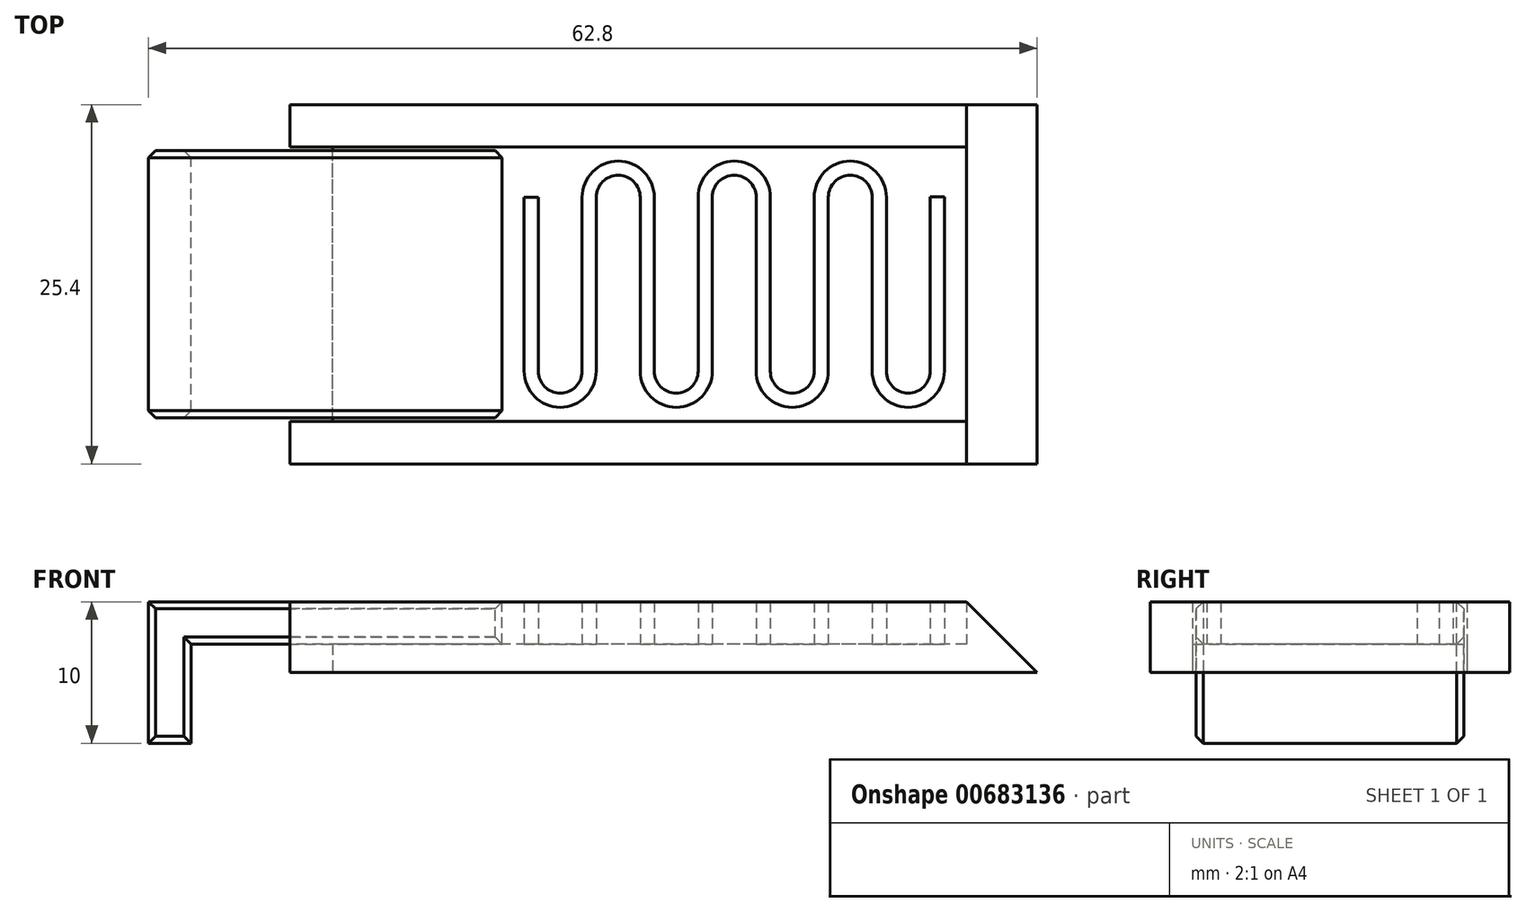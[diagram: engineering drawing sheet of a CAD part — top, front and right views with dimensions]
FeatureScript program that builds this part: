
annotation { "Feature Type Name" : "Feature", "Feature Type Description" : "" }
export const myFeature = defineFeature(function(context is Context, id is Id, definition is map)
    precondition{}
    {
        {
            var Q0;
            Q0=qCreatedBy(makeId("Top.planeOp"),FACE);
            var sketch = newSketch(context, id + "F0", { "sketchPlane" : qUnion([Q0])});
            skLineSegment(sketch, "E0.bottom", {"start": v(25.4, -12.7) * mm, "end": v(-25.4, -12.7) * mm});
            skLineSegment(sketch, "E0.top", {"start": v(25.4, 12.7) * mm, "end": v(-25.4, 12.7) * mm});
            skLineSegment(sketch, "E0.left", {"start": v(25.4, -12.7) * mm, "end": v(25.4, 12.7) * mm});
            skLineSegment(sketch, "E0.right", {"start": v(-25.4, -12.7) * mm, "end": v(-25.4, 12.7) * mm});
            skPoint(sketch, "E0.middle", {"position": v(0, 0) * mm});
            skSolve(sketch);
        }
        {
            var Q0;
            Q0=makeQuery(id+"F0.imprint","IMPRINT",FACE,{"disambiguationData":[TD([[makeQuery(id+"F0.imprint","IMPRINT",EDGE,{"derivedFrom":sQuery(id+"F0.wireOp",EDGE,"E0.bottom")}),-1.0]])]});
            extrude(context, id + "F1", {"entities" : qUnion([Q0]), "depth" : 2 * mm, "offsetDistance" : 25 * mm});
        }
        {
            var Q0;
            Q0=makeQuery(id+"F1.opExtrude","CAP_FACE",FACE,{"disambiguationData":[OSD([sQuery(id+"F0.wireOp",EDGE,"E0.bottom"),sQuery(id+"F0.wireOp",EDGE,"E0.top"),sQuery(id+"F0.wireOp",EDGE,"E0.left"),sQuery(id+"F0.wireOp",EDGE,"E0.right")])],"isStart":false});
            var sketch = newSketch(context, id + "F2", { "sketchPlane" : qUnion([Q0])});
            skLineSegment(sketch, "E1", {"start": v(-25.4, 9.7) * mm, "end": v(25.4, 9.7) * mm});
            skLineSegment(sketch, "E2", {"start": v(25.4, 9.7) * mm, "end": v(25.4, 9.7) * mm});
            skLineSegment(sketch, "E3", {"start": v(25.4, -9.7) * mm, "end": v(-25.4, -9.7) * mm});
            skSolve(sketch);
        }
        {
            var Q0;
            {var subQ0=sQuery(id+"F2.wireOp",EDGE,"E1");Q0=makeQuery(id+"F2.imprint","IMPRINT",FACE,{"disambiguationData":[TD([[makeQuery(id+"F2.imprint","IMPRINT",EDGE,{"derivedFrom":subQ0}),1.0]])]});}
            var Q1;
            {var subQ0=sQuery(id+"F2.wireOp",EDGE,"E3");Q1=makeQuery(id+"F2.imprint","IMPRINT",FACE,{"disambiguationData":[TD([[makeQuery(id+"F2.imprint","IMPRINT",EDGE,{"derivedFrom":subQ0}),1.0]])]});}
            extrude(context, id + "F3", {"entities" : qUnion([Q0, Q1]), "operationType" : NewBodyOperationType.ADD, "depth" : 3 * mm, "offsetDistance" : 25 * mm});
        }
        {
            var Q0;
            {var subQ0=sQuery(id+"F0.wireOp",EDGE,"E0.bottom");Q0=makeQuery(id+"F3.boolean.opBoolean","MERGE",FACE,{"derivedFrom":[makeQuery(id+"F1.opExtrude","SWEPT_FACE",FACE,{"disambiguationData":[OSD([subQ0])]}),makeQuery(id+"F3.opExtrude","SWEPT_FACE",FACE,{"disambiguationData":[OSD([subQ0])]})]});}
            var sketch = newSketch(context, id + "F4", { "sketchPlane" : qUnion([Q0])});
            skLineSegment(sketch, "E4", {"start": v(25.4, 5) * mm, "end": v(25.4, 0) * mm});
            skLineSegment(sketch, "E5", {"start": v(25.4, 5) * mm, "end": v(30.4, 0) * mm});
            skLineSegment(sketch, "E6", {"start": v(30.4, 0) * mm, "end": v(25.4, 0) * mm});
            skSolve(sketch);
        }
        {
            var Q0;
            Q0=makeQuery(id+"F4.imprint","IMPRINT",FACE,{"disambiguationData":[TD([[makeQuery(id+"F4.imprint","IMPRINT",EDGE,{"derivedFrom":sQuery(id+"F4.wireOp",EDGE,"E4")}),1.0]])]});
            extrude(context, id + "F5", {"entities" : qUnion([Q0]), "operationType" : NewBodyOperationType.ADD, "oppositeDirection" : true, "depth" : 25.4 * mm, "offsetDistance" : 25 * mm});
        }
        {
            var Q0;
            {var subQ0=sQuery(id+"F0.wireOp",EDGE,"E0.right");var subQ1=makeQuery(id+"F1.opExtrude","CAP_EDGE",EDGE,{"disambiguationData":[OSD([subQ0])],"isStart":false});Q0=makeQuery(id+"F3.boolean.opBoolean","MERGE",FACE,{"derivedFrom":[makeQuery(id+"F1.opExtrude","SWEPT_FACE",FACE,{"disambiguationData":[OSD([subQ0])]}),makeQuery(id+"F3.opExtrude","SWEPT_FACE",FACE,{"disambiguationData":[OSD([subQ0]),TDD([makeQuery(id+"F2.imprint","IMPRINT",EDGE,{"disambiguationData":[TD([[makeQuery(id+"F2.imprint","INTERSECT",VERTEX,{"derivedFrom":[makeQuery(id+"F1.opExtrude","CAP_EDGE",EDGE,{"disambiguationData":[OSD([sQuery(id+"F0.wireOp",EDGE,"E0.bottom")])],"isStart":false}),subQ1]}),-1.0]])],"derivedFrom":subQ1})])]}),makeQuery(id+"F3.opExtrude","SWEPT_FACE",FACE,{"disambiguationData":[OSD([subQ0]),TDD([makeQuery(id+"F2.imprint","IMPRINT",EDGE,{"disambiguationData":[TD([[makeQuery(id+"F2.imprint","INTERSECT",VERTEX,{"derivedFrom":[makeQuery(id+"F1.opExtrude","CAP_EDGE",EDGE,{"disambiguationData":[OSD([sQuery(id+"F0.wireOp",EDGE,"E0.top")])],"isStart":false}),subQ1]}),1.0]])],"derivedFrom":subQ1})])]})]});}
            extrude(context, id + "F6", {"entities" : qUnion([Q0]), "operationType" : NewBodyOperationType.REMOVE, "oppositeDirection" : true, "depth" : 3 * mm, "offsetDistance" : 25 * mm});
        }
        {
            var Q0;
            Q0=makeQuery(id+"F6.boolean.opBoolean","COPY",FACE,{"derivedFrom":makeQuery(id+"F6.opExtrude","CAP_FACE",FACE,{"disambiguationData":[OSD([sQuery(id+"F0.wireOp",EDGE,"E0.right")])],"isStart":false})});
            var sketch = newSketch(context, id + "F7", { "sketchPlane" : qUnion([Q0])});
            skLineSegment(sketch, "E7.bottom", {"start": v(9.7, 2) * mm, "end": v(-9.7, 2) * mm});
            skLineSegment(sketch, "E7.top", {"start": v(9.7, 0) * mm, "end": v(-9.7, 0) * mm});
            skLineSegment(sketch, "E7.left", {"start": v(9.7, 2) * mm, "end": v(9.7, 0) * mm});
            skLineSegment(sketch, "E7.right", {"start": v(-9.7, 2) * mm, "end": v(-9.7, 0) * mm});
            skSolve(sketch);
        }
        {
            var Q0;
            Q0 = qSketchRegion(id + "F7", true);
            extrude(context, id + "F8", {"entities" : qUnion([Q0]), "operationType" : NewBodyOperationType.REMOVE, "oppositeDirection" : true, "depth" : 3 * mm, "offsetDistance" : 25 * mm});
        }
        {
            var Q0;
            Q0=makeQuery(id+"F1.opExtrude","CAP_FACE",FACE,{"disambiguationData":[OSD([sQuery(id+"F0.wireOp",EDGE,"E0.bottom"),sQuery(id+"F0.wireOp",EDGE,"E0.top"),sQuery(id+"F0.wireOp",EDGE,"E0.left"),sQuery(id+"F0.wireOp",EDGE,"E0.right")])],"isStart":false});
            var sketch = newSketch(context, id + "F9", { "sketchPlane" : qUnion([Q0])});
            skLineSegment(sketch, "E8.bottom", {"start": v(-7.4, 9.45) * mm, "end": v(-32.4, 9.45) * mm});
            skLineSegment(sketch, "E8.top", {"start": v(-7.4, -9.45) * mm, "end": v(-32.4, -9.45) * mm});
            skLineSegment(sketch, "E8.left", {"start": v(-7.4, 9.45) * mm, "end": v(-7.4, -9.45) * mm});
            skLineSegment(sketch, "E8.right", {"start": v(-32.4, 9.45) * mm, "end": v(-32.4, -9.45) * mm});
            skSolve(sketch);
        }
        {
            var Q0;
            {var subQ0=sQuery(id+"F9.wireOp",EDGE,"E8.right");Q0=makeQuery(id+"F9.imprint","IMPRINT",FACE,{"disambiguationData":[TD([[makeQuery(id+"F9.imprint","IMPRINT",EDGE,{"derivedFrom":subQ0}),1.0]])]});}
            var Q1;
            {var subQ0=sQuery(id+"F9.wireOp",EDGE,"E8.left");Q1=makeQuery(id+"F9.imprint","IMPRINT",FACE,{"disambiguationData":[TD([[makeQuery(id+"F9.imprint","IMPRINT",EDGE,{"derivedFrom":subQ0}),-1.0]])]});}
            extrude(context, id + "F10", {"entities" : qUnion([Q0, Q1]), "depth" : 3 * mm, "offsetDistance" : 25 * mm});
        }
        {
            var Q0;
            Q0=makeQuery(id+"F10.opExtrude","CAP_FACE",FACE,{"disambiguationData":[OSD([sQuery(id+"F9.wireOp",EDGE,"E8.bottom"),sQuery(id+"F9.wireOp",EDGE,"E8.top"),sQuery(id+"F9.wireOp",EDGE,"E8.left"),sQuery(id+"F9.wireOp",EDGE,"E8.right")])],"isStart":true});
            var sketch = newSketch(context, id + "F11", { "sketchPlane" : qUnion([Q0])});
            skLineSegment(sketch, "E9.bottom", {"start": v(-32.4, 9.45) * mm, "end": v(-29.4, 9.45) * mm});
            skLineSegment(sketch, "E9.top", {"start": v(-32.4, -9.45) * mm, "end": v(-29.4, -9.45) * mm});
            skLineSegment(sketch, "E9.left", {"start": v(-32.4, 9.45) * mm, "end": v(-32.4, -9.45) * mm});
            skLineSegment(sketch, "E9.right", {"start": v(-29.4, 9.45) * mm, "end": v(-29.4, -9.45) * mm});
            skSolve(sketch);
        }
        {
            var Q0;
            Q0=makeQuery(id+"F11.imprint","IMPRINT",FACE,{"disambiguationData":[TD([[makeQuery(id+"F11.imprint","IMPRINT",EDGE,{"derivedFrom":sQuery(id+"F11.wireOp",EDGE,"E9.bottom")}),1.0]])]});
            extrude(context, id + "F12", {"entities" : qUnion([Q0]), "operationType" : NewBodyOperationType.ADD, "depth" : 7 * mm, "offsetDistance" : 25 * mm});
        }
        {
            var Q0;
            Q0=makeQuery(id+"F1.opExtrude","CAP_FACE",FACE,{"disambiguationData":[OSD([sQuery(id+"F0.wireOp",EDGE,"E0.bottom"),sQuery(id+"F0.wireOp",EDGE,"E0.top"),sQuery(id+"F0.wireOp",EDGE,"E0.left"),sQuery(id+"F0.wireOp",EDGE,"E0.right")])],"isStart":false});
            var sketch = newSketch(context, id + "F13", { "sketchPlane" : qUnion([Q0])});
            skLineSegment(sketch, "E10.bottom", {"start": v(25.4, -8.7) * mm, "end": v(-7.4, -8.7) * mm});
            skLineSegment(sketch, "E10.top", {"start": v(25.4, 8.7) * mm, "end": v(-7.4, 8.7) * mm});
            skLineSegment(sketch, "E10.left", {"start": v(25.4, -8.7) * mm, "end": v(25.4, 8.7) * mm});
            skLineSegment(sketch, "E10.right", {"start": v(-7.4, -8.7) * mm, "end": v(-7.4, 8.7) * mm});
            skPoint(sketch, "E10.middle", {"position": v(9, 0) * mm});
            skLineSegment(sketch, "E11", {"start": v(9, 0) * mm, "end": v(-7.4, 0) * mm, "construction": true});
            skLineSegment(sketch, "E12", {"start": v(0.8, 0) * mm, "end": v(0.8, 8.7) * mm, "construction": true});
            skLineSegment(sketch, "E13", {"start": v(0.8, 0) * mm, "end": v(0.8, -8.7) * mm, "construction": true});
            skCircle(sketch, "E14", {"center": v(9, 6.15) * mm, "radius": 2.55 * mm});
            skCircle(sketch, "E15", {"center": v(9, 6.15) * mm, "radius": 1.55 * mm});
            skCircle(sketch, "E16", {"center": v(0.8, 6.15) * mm, "radius": 2.55 * mm});
            skCircle(sketch, "E17", {"center": v(0.8, 6.15) * mm, "radius": 1.55 * mm});
            skCircle(sketch, "E18", {"center": v(17.2, 6.15) * mm, "radius": 2.55 * mm});
            skCircle(sketch, "E19", {"center": v(17.2, 6.15) * mm, "radius": 1.55 * mm});
            skCircle(sketch, "E20", {"center": v(4.9, -6.15) * mm, "radius": 2.55 * mm});
            skCircle(sketch, "E21", {"center": v(4.9, -6.15) * mm, "radius": 1.55 * mm});
            skCircle(sketch, "E22", {"center": v(13.1, -6.15) * mm, "radius": 2.55 * mm});
            skCircle(sketch, "E23", {"center": v(13.1, -6.15) * mm, "radius": 1.55 * mm});
            skCircle(sketch, "E24", {"center": v(-3.3, -6.15) * mm, "radius": 1.55 * mm});
            skCircle(sketch, "E25", {"center": v(-3.3, -6.15) * mm, "radius": 2.55 * mm});
            skLineSegment(sketch, "E26.bottom", {"start": v(0.8, 6.15) * mm, "end": v(0.8, 6.15) * mm});
            skLineSegment(sketch, "E26.top", {"start": v(0.8, 6.15) * mm, "end": v(0.8, 6.15) * mm});
            skLineSegment(sketch, "E26.left", {"start": v(0.8, 6.15) * mm, "end": v(0.8, 6.15) * mm});
            skLineSegment(sketch, "E26.right", {"start": v(0.8, 6.15) * mm, "end": v(0.8, 6.15) * mm});
            skLineSegment(sketch, "E27.bottom", {"start": v(-0.75, 6.15) * mm, "end": v(-1.75, 6.15) * mm});
            skLineSegment(sketch, "E27.top", {"start": v(-0.75, -6.15) * mm, "end": v(-1.75, -6.15) * mm});
            skLineSegment(sketch, "E27.left", {"start": v(-0.75, 6.15) * mm, "end": v(-0.75, -6.15) * mm});
            skLineSegment(sketch, "E27.right", {"start": v(-1.75, 6.15) * mm, "end": v(-1.75, -6.15) * mm});
            skLineSegment(sketch, "E28.bottom", {"start": v(2.35, 6.15) * mm, "end": v(3.35, 6.15) * mm});
            skLineSegment(sketch, "E28.top", {"start": v(2.35, -6.15) * mm, "end": v(3.35, -6.15) * mm});
            skLineSegment(sketch, "E28.left", {"start": v(2.35, 6.15) * mm, "end": v(2.35, -6.15) * mm});
            skLineSegment(sketch, "E28.right", {"start": v(3.35, 6.15) * mm, "end": v(3.35, -6.15) * mm});
            skLineSegment(sketch, "E29.bottom", {"start": v(7.45, 6.15) * mm, "end": v(6.45, 6.15) * mm});
            skLineSegment(sketch, "E29.top", {"start": v(7.45, -6.15) * mm, "end": v(6.45, -6.15) * mm});
            skLineSegment(sketch, "E29.left", {"start": v(7.45, 6.15) * mm, "end": v(7.45, -6.15) * mm});
            skLineSegment(sketch, "E29.right", {"start": v(6.45, 6.15) * mm, "end": v(6.45, -6.15) * mm});
            skLineSegment(sketch, "E30.bottom", {"start": v(10.55, 6.15) * mm, "end": v(11.55, 6.15) * mm});
            skLineSegment(sketch, "E30.top", {"start": v(10.55, -6.15) * mm, "end": v(11.55, -6.15) * mm});
            skLineSegment(sketch, "E30.left", {"start": v(10.55, 6.15) * mm, "end": v(10.55, -6.15) * mm});
            skLineSegment(sketch, "E30.right", {"start": v(11.55, 6.15) * mm, "end": v(11.55, -6.15) * mm});
            skLineSegment(sketch, "E31.bottom", {"start": v(15.65, 6.15) * mm, "end": v(14.65, 6.15) * mm});
            skLineSegment(sketch, "E31.top", {"start": v(15.65, -6.15) * mm, "end": v(14.65, -6.15) * mm});
            skLineSegment(sketch, "E31.left", {"start": v(15.65, 6.15) * mm, "end": v(15.65, -6.15) * mm});
            skLineSegment(sketch, "E31.right", {"start": v(14.65, 6.15) * mm, "end": v(14.65, -6.15) * mm});
            skLineSegment(sketch, "E32.bottom", {"start": v(18.75, 6.15) * mm, "end": v(19.75, 6.15) * mm});
            skLineSegment(sketch, "E32.top", {"start": v(18.75, -6.15) * mm, "end": v(19.75, -6.15) * mm});
            skLineSegment(sketch, "E32.left", {"start": v(18.75, 6.15) * mm, "end": v(18.75, -6.15) * mm});
            skLineSegment(sketch, "E32.right", {"start": v(19.75, 6.15) * mm, "end": v(19.75, -6.15) * mm});
            skLineSegment(sketch, "E33.bottom", {"start": v(-4.85, 6.15) * mm, "end": v(-5.85, 6.15) * mm});
            skLineSegment(sketch, "E33.top", {"start": v(-4.85, -6.15) * mm, "end": v(-5.85, -6.15) * mm});
            skLineSegment(sketch, "E33.left", {"start": v(-4.85, 6.15) * mm, "end": v(-4.85, -6.15) * mm});
            skLineSegment(sketch, "E33.right", {"start": v(-5.85, 6.15) * mm, "end": v(-5.85, -6.15) * mm});
            skLineSegment(sketch, "E34.bottom", {"start": v(-7.4, 8.7) * mm, "end": v(-5.85, 8.7) * mm});
            skLineSegment(sketch, "E34.top", {"start": v(-7.4, 3.6) * mm, "end": v(-5.85, 3.6) * mm});
            skLineSegment(sketch, "E34.left", {"start": v(-7.4, 8.7) * mm, "end": v(-7.4, 3.6) * mm});
            skLineSegment(sketch, "E34.right", {"start": v(-5.85, 8.7) * mm, "end": v(-5.85, 3.6) * mm});
            skCircle(sketch, "E35", {"center": v(21.3, -6.15) * mm, "radius": 2.55 * mm});
            skCircle(sketch, "E36", {"center": v(21.3, -6.15) * mm, "radius": 1.55 * mm});
            skLineSegment(sketch, "E37.bottom", {"start": v(22.85, -6.15) * mm, "end": v(23.85, -6.15) * mm});
            skLineSegment(sketch, "E37.top", {"start": v(22.85, 6.16) * mm, "end": v(23.85, 6.16) * mm});
            skLineSegment(sketch, "E37.left", {"start": v(22.85, -6.15) * mm, "end": v(22.85, 6.16) * mm});
            skLineSegment(sketch, "E37.right", {"start": v(23.85, -6.15) * mm, "end": v(23.85, 6.16) * mm});
            skLineSegment(sketch, "E38.bottom", {"start": v(23.85, 6.16) * mm, "end": v(23.85, 6.16) * mm});
            skLineSegment(sketch, "E38.top", {"start": v(23.85, 6.16) * mm, "end": v(23.85, 6.16) * mm});
            skLineSegment(sketch, "E38.left", {"start": v(23.85, 6.16) * mm, "end": v(23.85, 6.16) * mm});
            skLineSegment(sketch, "E38.right", {"start": v(23.85, 6.16) * mm, "end": v(23.85, 6.16) * mm});
            skLineSegment(sketch, "E39.bottom", {"start": v(25.4, 8.7) * mm, "end": v(23.85, 8.7) * mm});
            skLineSegment(sketch, "E39.top", {"start": v(25.4, 3.6) * mm, "end": v(23.85, 3.6) * mm});
            skLineSegment(sketch, "E39.left", {"start": v(25.4, 8.7) * mm, "end": v(25.4, 3.6) * mm});
            skLineSegment(sketch, "E39.right", {"start": v(23.85, 8.7) * mm, "end": v(23.85, 3.6) * mm});
            skSolve(sketch);
        }
        {
            var Q0;
            {var subQ1=sQuery(id+"F13.wireOp",EDGE,"E34.bottom");Q0=makeQuery(id+"F13.imprint","IMPRINT",FACE,{"disambiguationData":[TD([[makeQuery(id+"F13.imprint","IMPRINT",EDGE,{"derivedFrom":subQ1}),-1.0]])]});}
            var Q1;
            {var subQ2=sQuery(id+"F13.wireOp",EDGE,"E33.bottom");Q1=makeQuery(id+"F13.imprint","IMPRINT",FACE,{"disambiguationData":[TD([[makeQuery(id+"F13.imprint","IMPRINT",EDGE,{"derivedFrom":subQ2}),1.0]])]});}
            var Q2;
            {var subQ1=sQuery(id+"F13.wireOp",EDGE,"E16");var subQ3=sQuery(id+"F13.wireOp",EDGE,"E27.left");var subQ4=makeQuery(id+"F13.imprint","INTERSECT",VERTEX,{"derivedFrom":[subQ1,subQ3]});Q2=makeQuery(id+"F13.imprint","IMPRINT",FACE,{"disambiguationData":[TD([[makeQuery(id+"F13.imprint","IMPRINT",EDGE,{"disambiguationData":[TD([[subQ4,1.0]])],"derivedFrom":subQ1}),-1.0]])]});}
            var Q3;
            {var subQ0=sQuery(id+"F13.wireOp",EDGE,"E33.top");Q3=makeQuery(id+"F13.imprint","IMPRINT",FACE,{"disambiguationData":[TD([[makeQuery(id+"F13.imprint","IMPRINT",EDGE,{"derivedFrom":subQ0}),-1.0]])]});}
            var Q4;
            {var subQ0=sQuery(id+"F13.wireOp",EDGE,"E27.top");Q4=makeQuery(id+"F13.imprint","IMPRINT",FACE,{"disambiguationData":[TD([[makeQuery(id+"F13.imprint","IMPRINT",EDGE,{"derivedFrom":subQ0}),-1.0]])]});}
            var Q5;
            {var subQ0=sQuery(id+"F13.wireOp",EDGE,"E27.top");Q5=makeQuery(id+"F13.imprint","IMPRINT",FACE,{"disambiguationData":[TD([[makeQuery(id+"F13.imprint","IMPRINT",EDGE,{"derivedFrom":subQ0}),1.0]])]});}
            var Q6;
            {var subQ0=sQuery(id+"F13.wireOp",EDGE,"E27.bottom");Q6=makeQuery(id+"F13.imprint","IMPRINT",FACE,{"disambiguationData":[TD([[makeQuery(id+"F13.imprint","IMPRINT",EDGE,{"derivedFrom":subQ0}),-1.0]])]});}
            var Q7;
            {var subQ0=sQuery(id+"F13.wireOp",EDGE,"E27.bottom");Q7=makeQuery(id+"F13.imprint","IMPRINT",FACE,{"disambiguationData":[TD([[makeQuery(id+"F13.imprint","IMPRINT",EDGE,{"derivedFrom":subQ0}),1.0]])]});}
            var Q8;
            {var subQ0=sQuery(id+"F13.wireOp",EDGE,"E28.bottom");Q8=makeQuery(id+"F13.imprint","IMPRINT",FACE,{"disambiguationData":[TD([[makeQuery(id+"F13.imprint","IMPRINT",EDGE,{"derivedFrom":subQ0}),-1.0]])]});}
            var Q9;
            {var subQ1=sQuery(id+"F13.wireOp",EDGE,"E16");var subQ3=sQuery(id+"F13.wireOp",EDGE,"E28.left");var subQ4=makeQuery(id+"F13.imprint","INTERSECT",VERTEX,{"derivedFrom":[subQ1,subQ3]});Q9=makeQuery(id+"F13.imprint","IMPRINT",FACE,{"disambiguationData":[TD([[makeQuery(id+"F13.imprint","IMPRINT",EDGE,{"disambiguationData":[TD([[subQ4,-1.0]])],"derivedFrom":subQ1}),-1.0]])]});}
            var Q10;
            {var subQ0=sQuery(id+"F13.wireOp",EDGE,"E28.top");Q10=makeQuery(id+"F13.imprint","IMPRINT",FACE,{"disambiguationData":[TD([[makeQuery(id+"F13.imprint","IMPRINT",EDGE,{"derivedFrom":subQ0}),-1.0]])]});}
            var Q11;
            {var subQ1=sQuery(id+"F13.wireOp",EDGE,"E14");var subQ3=sQuery(id+"F13.wireOp",EDGE,"E29.left");var subQ4=makeQuery(id+"F13.imprint","INTERSECT",VERTEX,{"derivedFrom":[subQ1,subQ3]});Q11=makeQuery(id+"F13.imprint","IMPRINT",FACE,{"disambiguationData":[TD([[makeQuery(id+"F13.imprint","IMPRINT",EDGE,{"disambiguationData":[TD([[subQ4,1.0]])],"derivedFrom":subQ1}),-1.0]])]});}
            var Q12;
            {var subQ0=sQuery(id+"F13.wireOp",EDGE,"E29.bottom");Q12=makeQuery(id+"F13.imprint","IMPRINT",FACE,{"disambiguationData":[TD([[makeQuery(id+"F13.imprint","IMPRINT",EDGE,{"derivedFrom":subQ0}),-1.0]])]});}
            var Q13;
            {var subQ0=sQuery(id+"F13.wireOp",EDGE,"E29.bottom");Q13=makeQuery(id+"F13.imprint","IMPRINT",FACE,{"disambiguationData":[TD([[makeQuery(id+"F13.imprint","IMPRINT",EDGE,{"derivedFrom":subQ0}),1.0]])]});}
            var Q14;
            {var subQ0=sQuery(id+"F13.wireOp",EDGE,"E28.top");Q14=makeQuery(id+"F13.imprint","IMPRINT",FACE,{"disambiguationData":[TD([[makeQuery(id+"F13.imprint","IMPRINT",EDGE,{"derivedFrom":subQ0}),1.0]])]});}
            var Q15;
            {var subQ0=sQuery(id+"F13.wireOp",EDGE,"E29.top");Q15=makeQuery(id+"F13.imprint","IMPRINT",FACE,{"disambiguationData":[TD([[makeQuery(id+"F13.imprint","IMPRINT",EDGE,{"derivedFrom":subQ0}),-1.0]])]});}
            var Q16;
            {var subQ0=sQuery(id+"F13.wireOp",EDGE,"E30.bottom");Q16=makeQuery(id+"F13.imprint","IMPRINT",FACE,{"disambiguationData":[TD([[makeQuery(id+"F13.imprint","IMPRINT",EDGE,{"derivedFrom":subQ0}),-1.0]])]});}
            var Q17;
            {var subQ1=sQuery(id+"F13.wireOp",EDGE,"E14");var subQ3=sQuery(id+"F13.wireOp",EDGE,"E30.left");var subQ4=makeQuery(id+"F13.imprint","INTERSECT",VERTEX,{"derivedFrom":[subQ1,subQ3]});Q17=makeQuery(id+"F13.imprint","IMPRINT",FACE,{"disambiguationData":[TD([[makeQuery(id+"F13.imprint","IMPRINT",EDGE,{"disambiguationData":[TD([[subQ4,-1.0]])],"derivedFrom":subQ1}),-1.0]])]});}
            var Q18;
            {var subQ0=sQuery(id+"F13.wireOp",EDGE,"E30.top");Q18=makeQuery(id+"F13.imprint","IMPRINT",FACE,{"disambiguationData":[TD([[makeQuery(id+"F13.imprint","IMPRINT",EDGE,{"derivedFrom":subQ0}),-1.0]])]});}
            var Q19;
            {var subQ0=sQuery(id+"F13.wireOp",EDGE,"E30.top");Q19=makeQuery(id+"F13.imprint","IMPRINT",FACE,{"disambiguationData":[TD([[makeQuery(id+"F13.imprint","IMPRINT",EDGE,{"derivedFrom":subQ0}),1.0]])]});}
            var Q20;
            {var subQ0=sQuery(id+"F13.wireOp",EDGE,"E31.top");Q20=makeQuery(id+"F13.imprint","IMPRINT",FACE,{"disambiguationData":[TD([[makeQuery(id+"F13.imprint","IMPRINT",EDGE,{"derivedFrom":subQ0}),-1.0]])]});}
            var Q21;
            {var subQ1=sQuery(id+"F13.wireOp",EDGE,"E18");var subQ3=sQuery(id+"F13.wireOp",EDGE,"E31.left");var subQ4=makeQuery(id+"F13.imprint","INTERSECT",VERTEX,{"derivedFrom":[subQ1,subQ3]});Q21=makeQuery(id+"F13.imprint","IMPRINT",FACE,{"disambiguationData":[TD([[makeQuery(id+"F13.imprint","IMPRINT",EDGE,{"disambiguationData":[TD([[subQ4,1.0]])],"derivedFrom":subQ1}),-1.0]])]});}
            var Q22;
            {var subQ0=sQuery(id+"F13.wireOp",EDGE,"E31.bottom");Q22=makeQuery(id+"F13.imprint","IMPRINT",FACE,{"disambiguationData":[TD([[makeQuery(id+"F13.imprint","IMPRINT",EDGE,{"derivedFrom":subQ0}),1.0]])]});}
            var Q23;
            {var subQ0=sQuery(id+"F13.wireOp",EDGE,"E32.bottom");Q23=makeQuery(id+"F13.imprint","IMPRINT",FACE,{"disambiguationData":[TD([[makeQuery(id+"F13.imprint","IMPRINT",EDGE,{"derivedFrom":subQ0}),-1.0]])]});}
            var Q24;
            {var subQ0=sQuery(id+"F13.wireOp",EDGE,"E31.bottom");Q24=makeQuery(id+"F13.imprint","IMPRINT",FACE,{"disambiguationData":[TD([[makeQuery(id+"F13.imprint","IMPRINT",EDGE,{"derivedFrom":subQ0}),-1.0]])]});}
            var Q25;
            {var subQ1=sQuery(id+"F13.wireOp",EDGE,"E39.bottom");Q25=makeQuery(id+"F13.imprint","IMPRINT",FACE,{"disambiguationData":[TD([[makeQuery(id+"F13.imprint","IMPRINT",EDGE,{"derivedFrom":subQ1}),1.0]])]});}
            var Q26;
            {var subQ1=sQuery(id+"F13.wireOp",EDGE,"E18");var subQ3=sQuery(id+"F13.wireOp",EDGE,"E32.left");var subQ4=makeQuery(id+"F13.imprint","INTERSECT",VERTEX,{"derivedFrom":[subQ1,subQ3]});Q26=makeQuery(id+"F13.imprint","IMPRINT",FACE,{"disambiguationData":[TD([[makeQuery(id+"F13.imprint","IMPRINT",EDGE,{"disambiguationData":[TD([[subQ4,-1.0]])],"derivedFrom":subQ1}),-1.0]])]});}
            var Q27;
            {var subQ0=sQuery(id+"F13.wireOp",EDGE,"E32.top");Q27=makeQuery(id+"F13.imprint","IMPRINT",FACE,{"disambiguationData":[TD([[makeQuery(id+"F13.imprint","IMPRINT",EDGE,{"derivedFrom":subQ0}),1.0]])]});}
            var Q28;
            {var subQ0=sQuery(id+"F13.wireOp",EDGE,"E37.bottom");Q28=makeQuery(id+"F13.imprint","IMPRINT",FACE,{"disambiguationData":[TD([[makeQuery(id+"F13.imprint","IMPRINT",EDGE,{"derivedFrom":subQ0}),1.0]])]});}
            var Q29;
            {var subQ1=sQuery(id+"F13.wireOp",EDGE,"E32.top");Q29=makeQuery(id+"F13.imprint","IMPRINT",FACE,{"disambiguationData":[TD([[makeQuery(id+"F13.imprint","IMPRINT",EDGE,{"derivedFrom":subQ1}),-1.0]])]});}
            var Q30;
            {var subQ4=sQuery(id+"F13.wireOp",EDGE,"E37.top");Q30=makeQuery(id+"F13.imprint","IMPRINT",FACE,{"disambiguationData":[TD([[makeQuery(id+"F13.imprint","IMPRINT",EDGE,{"derivedFrom":subQ4}),-1.0]])]});}
            extrude(context, id + "F14", {"entities" : qUnion([Q0, Q1, Q2, Q3, Q4, Q5, Q6, Q7, Q8, Q9, Q10, Q11, Q12, Q13, Q14, Q15, Q16, Q17, Q18, Q19, Q20, Q21, Q22, Q23, Q24, Q25, Q26, Q27, Q28, Q29, Q30]), "depth" : 3 * mm, "offsetDistance" : 25 * mm});
        }
        {
            var Q0;
            Q0=makeQuery(id+"F12.boolean.opBoolean","MERGE",FACE,{"derivedFrom":[makeQuery(id+"F10.opExtrude","SWEPT_FACE",FACE,{"disambiguationData":[OSD([sQuery(id+"F9.wireOp",EDGE,"E8.bottom")])]}),makeQuery(id+"F12.opExtrude","SWEPT_FACE",FACE,{"disambiguationData":[OSD([sQuery(id+"F11.wireOp",EDGE,"E9.top")])]})]});
            var Q1;
            Q1=makeQuery(id+"F12.boolean.opBoolean","MERGE",FACE,{"derivedFrom":[makeQuery(id+"F10.opExtrude","SWEPT_FACE",FACE,{"disambiguationData":[OSD([sQuery(id+"F9.wireOp",EDGE,"E8.top")])]}),makeQuery(id+"F12.opExtrude","SWEPT_FACE",FACE,{"disambiguationData":[OSD([sQuery(id+"F11.wireOp",EDGE,"E9.bottom")])]})]});
            chamfer(context, id + "F15", {"entities" : qUnion([Q0, Q1]), "width" : 0.5 * mm, "tangentPropagation" : true});
        }
    });
